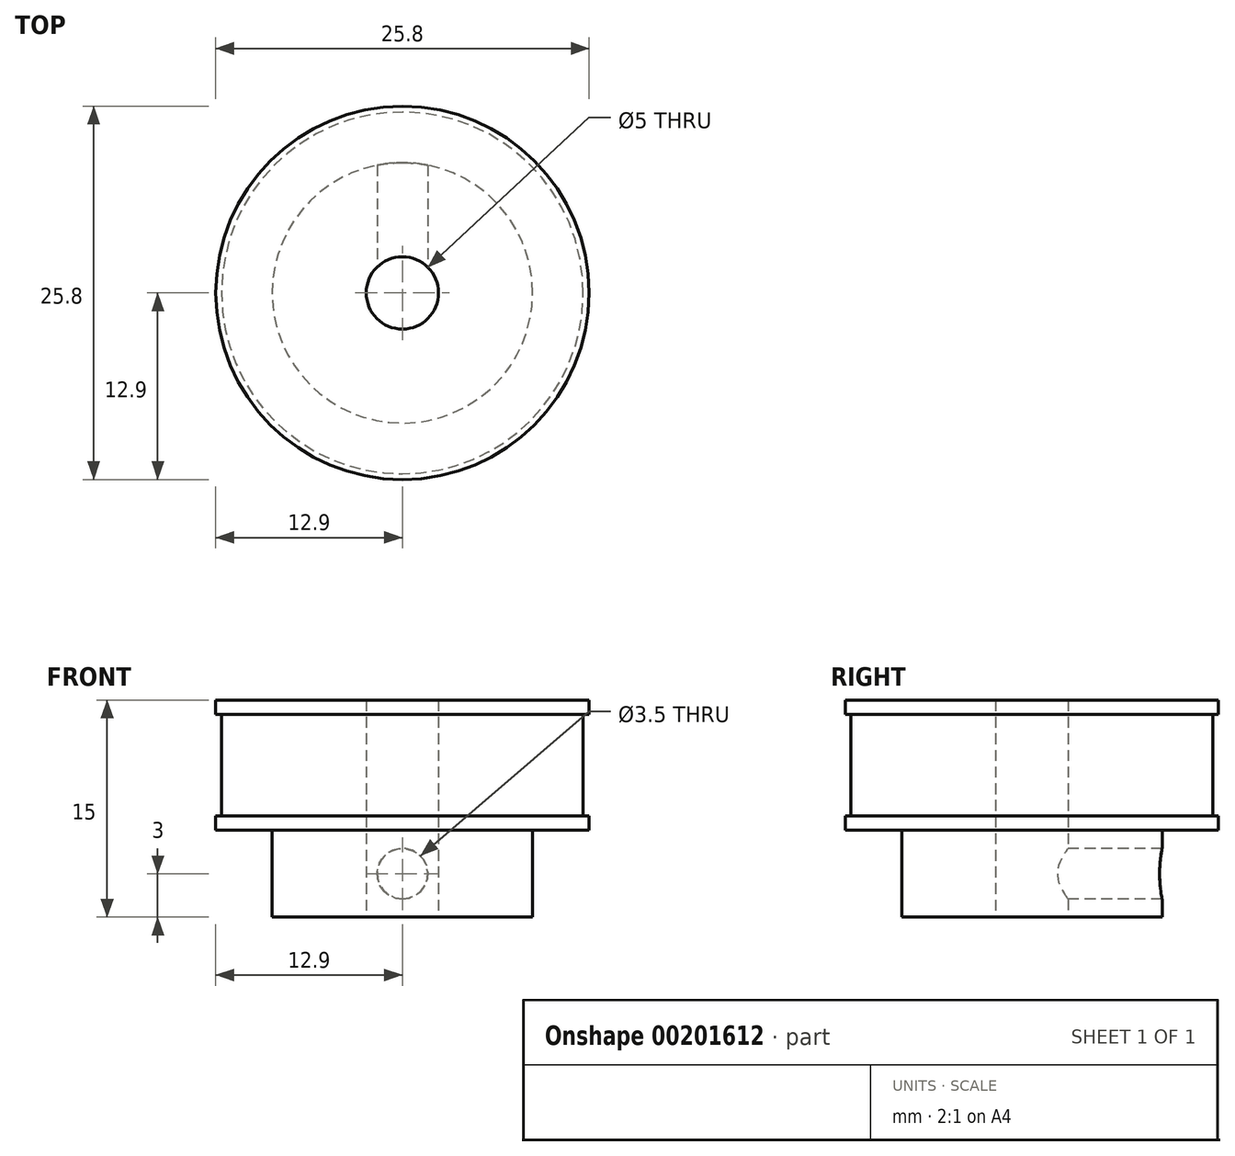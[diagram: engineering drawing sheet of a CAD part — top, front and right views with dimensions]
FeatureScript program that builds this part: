
annotation { "Feature Type Name" : "Feature", "Feature Type Description" : "" }
export const myFeature = defineFeature(function(context is Context, id is Id, definition is map)
    precondition{}
    {
        {
            var Q0;
            Q0=qCreatedBy(makeId("Top.planeOp"),FACE);
            var sketch = newSketch(context, id + "F0", { "sketchPlane" : qUnion([Q0])});
            skCircle(sketch, "E0", {"center": v(0, 0) * mm, "radius": 12.9 * mm});
            skSolve(sketch);
        }
        {
            var Q0;
            Q0=makeQuery(id+"F0.imprint","IMPRINT",FACE,{"disambiguationData":[TD([[makeQuery(id+"F0.imprint","IMPRINT",EDGE,{"derivedFrom":sQuery(id+"F0.wireOp",EDGE,"E0")}),1.0]])]});
            extrude(context, id + "F1", {"entities" : qUnion([Q0]), "depth" : 9 * mm});
        }
        {
            var Q0;
            Q0=makeQuery(id+"F1.opExtrude","CAP_FACE",FACE,{"disambiguationData":[OSD([sQuery(id+"F0.wireOp",EDGE,"E0")])],"isStart":true});
            var sketch = newSketch(context, id + "F2", { "sketchPlane" : qUnion([Q0])});
            skCircle(sketch, "E1", {"center": v(0, 0) * mm, "radius": 9 * mm});
            skSolve(sketch);
        }
        {
            var Q0;
            Q0=makeQuery(id+"F2.imprint","IMPRINT",FACE,{"disambiguationData":[TD([[makeQuery(id+"F2.imprint","IMPRINT",EDGE,{"derivedFrom":sQuery(id+"F2.wireOp",EDGE,"E1")}),1.0]])]});
            extrude(context, id + "F3", {"entities" : qUnion([Q0]), "operationType" : NewBodyOperationType.ADD, "depth" : 6 * mm});
        }
        {
            var Q0;
            Q0=makeQuery(id+"F3.opExtrude","CAP_FACE",FACE,{"disambiguationData":[OSD([sQuery(id+"F2.wireOp",EDGE,"E1")])],"isStart":false});
            var sketch = newSketch(context, id + "F4", { "sketchPlane" : qUnion([Q0])});
            skCircle(sketch, "E2", {"center": v(0, 0) * mm, "radius": 2.5 * mm});
            skSolve(sketch);
        }
        {
            var Q0;
            Q0=makeQuery(id+"F4.imprint","IMPRINT",FACE,{"disambiguationData":[TD([[makeQuery(id+"F4.imprint","IMPRINT",EDGE,{"derivedFrom":sQuery(id+"F4.wireOp",EDGE,"E2")}),1.0]])]});
            extrude(context, id + "F5", {"entities" : qUnion([Q0]), "operationType" : NewBodyOperationType.REMOVE, "oppositeDirection" : true, "depth" : 25 * mm});
        }
        {
            var Q0;
            Q0=qCreatedBy(makeId("Front.planeOp"),FACE);
            var sketch = newSketch(context, id + "F6", { "sketchPlane" : qUnion([Q0])});
            skLineSegment(sketch, "E3.bottom", {"start": v(-14.07, 8) * mm, "end": v(-12.5, 8) * mm});
            skLineSegment(sketch, "E3.top", {"start": v(-14.07, 1) * mm, "end": v(-12.5, 1) * mm});
            skLineSegment(sketch, "E3.left", {"start": v(-14.07, 8) * mm, "end": v(-14.07, 1) * mm});
            skLineSegment(sketch, "E3.right", {"start": v(-12.5, 8) * mm, "end": v(-12.5, 1) * mm});
            skSolve(sketch);
        }
        {
            var Q0;
            Q0=makeQuery(id+"F6.imprint","IMPRINT",FACE,{"disambiguationData":[TD([[makeQuery(id+"F6.imprint","IMPRINT",EDGE,{"derivedFrom":sQuery(id+"F6.wireOp",EDGE,"E3.bottom")}),-1.0]])]});
            var Q1;
            Q1=makeQuery(id+"F5.boolean.opBoolean","INTERSECT",EDGE,{"derivedFrom":[makeQuery(id+"F1.opExtrude","CAP_FACE",FACE,{"disambiguationData":[OSD([sQuery(id+"F0.wireOp",EDGE,"E0")])],"isStart":false}),makeQuery(id+"F5.opExtrude","SWEPT_FACE",FACE,{"disambiguationData":[OSD([sQuery(id+"F4.wireOp",EDGE,"E2")])]})]});
            revolve(context, id + "F7", {"operationType" : NewBodyOperationType.REMOVE, "entities" : qUnion([Q0]), "axis" : qUnion([Q1]), "revolveType" : RevolveType.FULL, "oppositeDirection" : true});
        }
        {
            var Q0;
            Q0=qCreatedBy(makeId("Front.planeOp"),FACE);
            var sketch = newSketch(context, id + "F8", { "sketchPlane" : qUnion([Q0])});
            skCircle(sketch, "E4", {"center": v(0, -3) * mm, "radius": 1.75 * mm});
            skSolve(sketch);
        }
        {
            var Q0;
            Q0=makeQuery(id+"F8.imprint","IMPRINT",FACE,{"disambiguationData":[TD([[makeQuery(id+"F8.imprint","IMPRINT",EDGE,{"derivedFrom":sQuery(id+"F8.wireOp",EDGE,"E4")}),1.0]])]});
            extrude(context, id + "F9", {"entities" : qUnion([Q0]), "operationType" : NewBodyOperationType.REMOVE, "oppositeDirection" : true, "depth" : 25 * mm});
        }
    });
